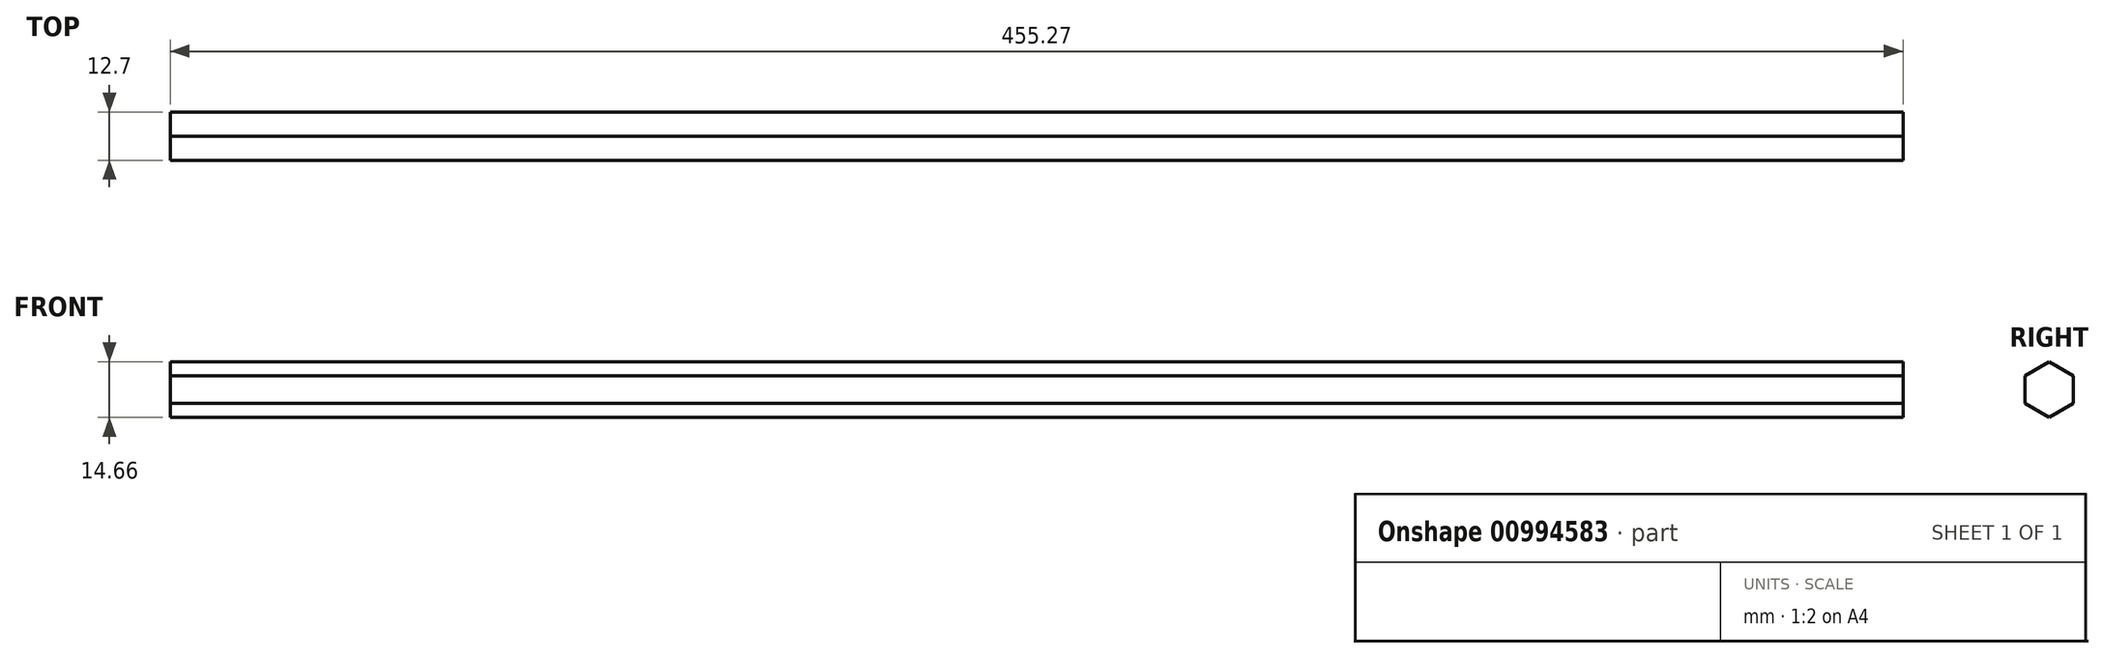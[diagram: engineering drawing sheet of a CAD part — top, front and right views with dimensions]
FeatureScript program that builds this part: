
annotation { "Feature Type Name" : "Feature", "Feature Type Description" : "" }
export const myFeature = defineFeature(function(context is Context, id is Id, definition is map)
    precondition{}
    {
        {
            var Q0;
            Q0=qCreatedBy(makeId("Right.planeOp"),FACE);
            var sketch = newSketch(context, id + "F0", { "sketchPlane" : qUnion([Q0])});
            skCircle(sketch, "E0.cCircle", {"center": v(0, 0) * mm, "radius": 6.35 * mm, "construction": true});
            skLineSegment(sketch, "E0.0", {"start": v(-6.35, -3.67) * mm, "end": v(-6.35, 3.67) * mm});
            skLineSegment(sketch, "E0.1", {"start": v(-6.35, 3.67) * mm, "end": v(0, 7.33) * mm});
            skLineSegment(sketch, "E0.2", {"start": v(0, 7.33) * mm, "end": v(6.35, 3.67) * mm});
            skLineSegment(sketch, "E0.3", {"start": v(6.35, 3.67) * mm, "end": v(6.35, -3.67) * mm});
            skLineSegment(sketch, "E0.4", {"start": v(6.35, -3.67) * mm, "end": v(0, -7.33) * mm});
            skLineSegment(sketch, "E0.5", {"start": v(0, -7.33) * mm, "end": v(-6.35, -3.67) * mm});
            skPoint(sketch, "E0.0.midPoint", {"position": v(-6.35, 0) * mm});
            skSolve(sketch);
        }
        {
            var Q0;
            Q0=makeQuery(id+"F0.imprint","IMPRINT",FACE,{"disambiguationData":[TD([[makeQuery(id+"F0.imprint","IMPRINT",EDGE,{"derivedFrom":sQuery(id+"F0.wireOp",EDGE,"E0.0")}),-1.0]])]});
            extrude(context, id + "F1", {"entities" : qUnion([Q0]), "depth" : 455.27 * mm, "offsetDistance" : 25.4 * mm});
        }
    });
